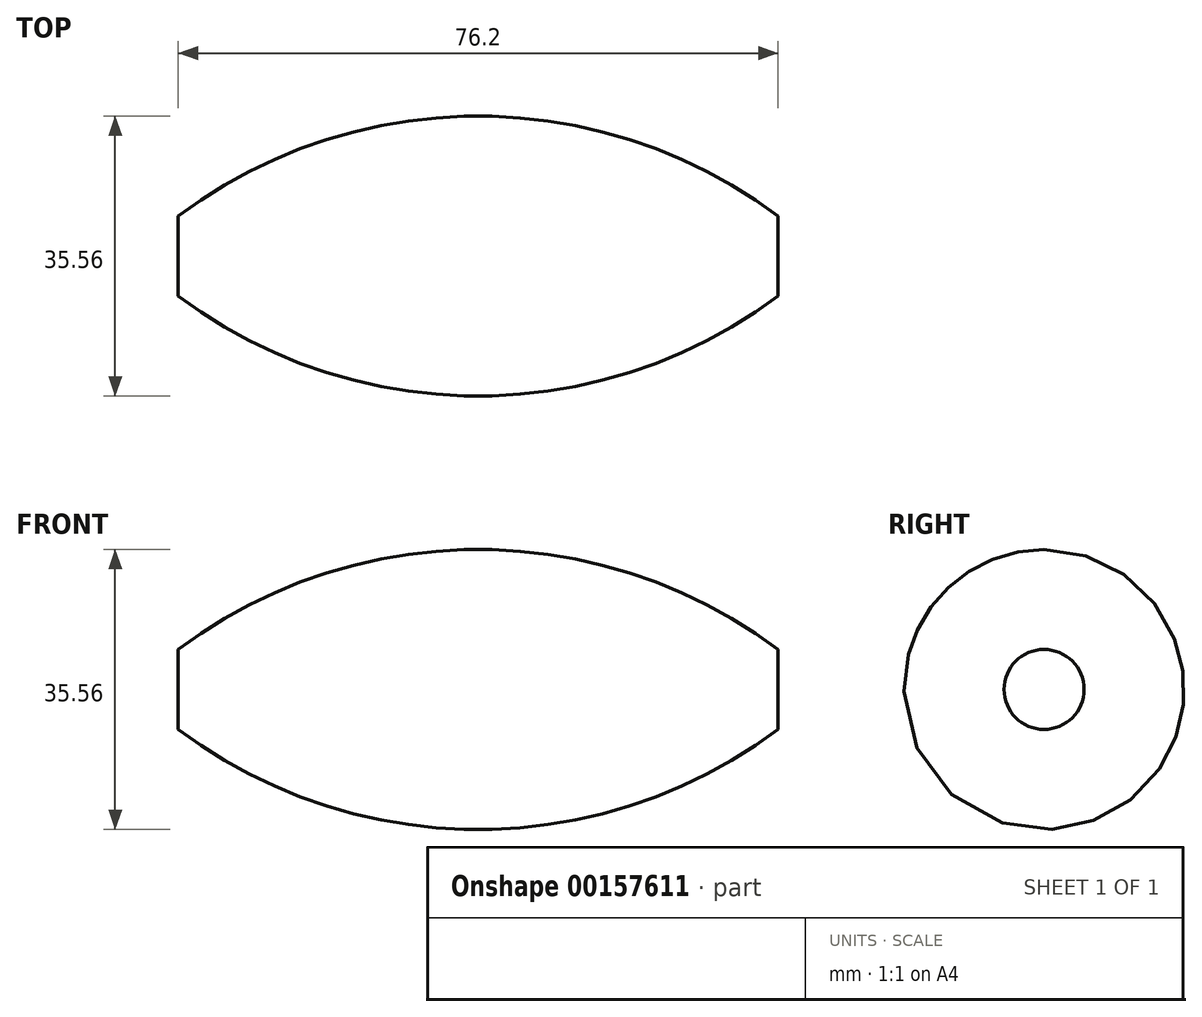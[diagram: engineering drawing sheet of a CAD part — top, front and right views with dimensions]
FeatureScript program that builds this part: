
annotation { "Feature Type Name" : "Feature", "Feature Type Description" : "" }
export const myFeature = defineFeature(function(context is Context, id is Id, definition is map)
    precondition{}
    {
        {
            var Q0;
            Q0=qCreatedBy(makeId("Front.planeOp"),FACE);
            var sketch = newSketch(context, id + "F0", { "sketchPlane" : qUnion([Q0])});
            skLineSegment(sketch, "E0", {"start": v(-76.2, 0) * mm, "end": v(0, 0) * mm});
            skLineSegment(sketch, "E1", {"start": v(-76.2, 0) * mm, "end": v(-76.2, 5.08) * mm});
            skLineSegment(sketch, "E2", {"start": v(0, 0) * mm, "end": v(0, 5.08) * mm});
            skArc(sketch, "E3", {"start": v(0, 5.08) * mm, "mid": v(-38.1, 17.78) * mm, "end": v(-76.2, 5.08) * mm});
            skSolve(sketch);
        }
        {
            var Q0;
            Q0=makeQuery(id+"F0.imprint","IMPRINT",FACE,{"disambiguationData":[TD([[makeQuery(id+"F0.imprint","IMPRINT",EDGE,{"derivedFrom":sQuery(id+"F0.wireOp",EDGE,"E0")}),1.0]])]});
            var Q1;
            Q1=sQuery(id+"F0.wireOp",EDGE,"E0");
            revolve(context, id + "F1", {"entities" : qUnion([Q0]), "axis" : qUnion([Q1]), "revolveType" : RevolveType.FULL});
        }
    });
